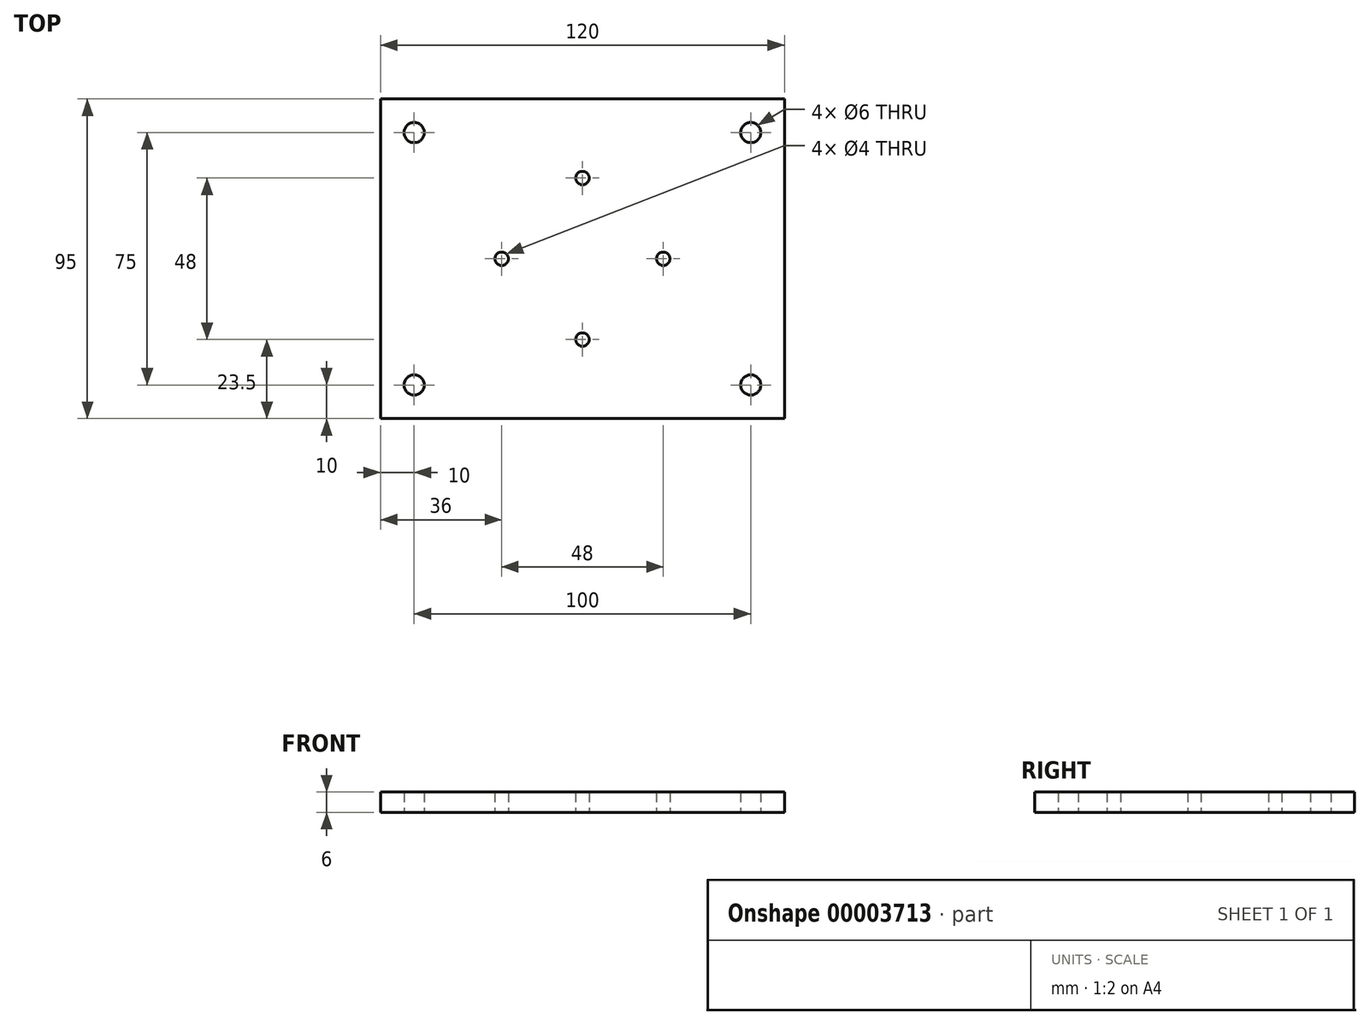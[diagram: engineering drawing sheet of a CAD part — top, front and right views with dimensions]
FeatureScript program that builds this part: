
annotation { "Feature Type Name" : "Feature", "Feature Type Description" : "" }
export const myFeature = defineFeature(function(context is Context, id is Id, definition is map)
    precondition{}
    {
        {
            var Q0;
            Q0=qCreatedBy(makeId("Top.planeOp"),FACE);
            var sketch = newSketch(context, id + "F0", { "sketchPlane" : qUnion([Q0])});
            skCircle(sketch, "E0", {"center": v(-50, 37.5) * mm, "radius": 3 * mm});
            skLineSegment(sketch, "E1.bottom", {"start": v(-60, 47.5) * mm, "end": v(60, 47.5) * mm});
            skLineSegment(sketch, "E1.top", {"start": v(-60, -47.5) * mm, "end": v(60, -47.5) * mm});
            skLineSegment(sketch, "E1.left", {"start": v(-60, 47.5) * mm, "end": v(-60, -47.5) * mm});
            skLineSegment(sketch, "E1.right", {"start": v(60, 47.5) * mm, "end": v(60, -47.5) * mm});
            skCircle(sketch, "E2", {"center": v(0, 24) * mm, "radius": 2 * mm});
            skCircle(sketch, "E3.1.0", {"center": v(-24, 0) * mm, "radius": 2 * mm});
            skCircle(sketch, "E3.2.0", {"center": v(0, -24) * mm, "radius": 2 * mm});
            skCircle(sketch, "E3.3.0", {"center": v(24, 0) * mm, "radius": 2 * mm});
            skPoint(sketch, "E3.center", {"position": v(0, 0) * mm});
            skCircle(sketch, "E4.0.1.0", {"center": v(-50, -37.5) * mm, "radius": 3 * mm});
            skCircle(sketch, "E4.1.0.0", {"center": v(50, 37.5) * mm, "radius": 3 * mm});
            skCircle(sketch, "E4.1.1.0", {"center": v(50, -37.5) * mm, "radius": 3 * mm});
            skLineSegment(sketch, "E4.direction1", {"start": v(-50, 37.5) * mm, "end": v(50, 37.5) * mm, "construction": true});
            skLineSegment(sketch, "E4.direction2", {"start": v(-50, 37.5) * mm, "end": v(-50, -37.5) * mm, "construction": true});
            skPoint(sketch, "E5", {"position": v(-50, 0) * mm});
            skSolve(sketch);
        }
        {
            var Q0;
            Q0=makeQuery(id+"F0.imprint","IMPRINT",FACE,{"disambiguationData":[TD([[makeQuery(id+"F0.imprint","IMPRINT",EDGE,{"derivedFrom":sQuery(id+"F0.wireOp",EDGE,"E0")}),-1.0]])]});
            extrude(context, id + "F1", {"entities" : qUnion([Q0]), "depth" : 6 * mm});
        }
    });
